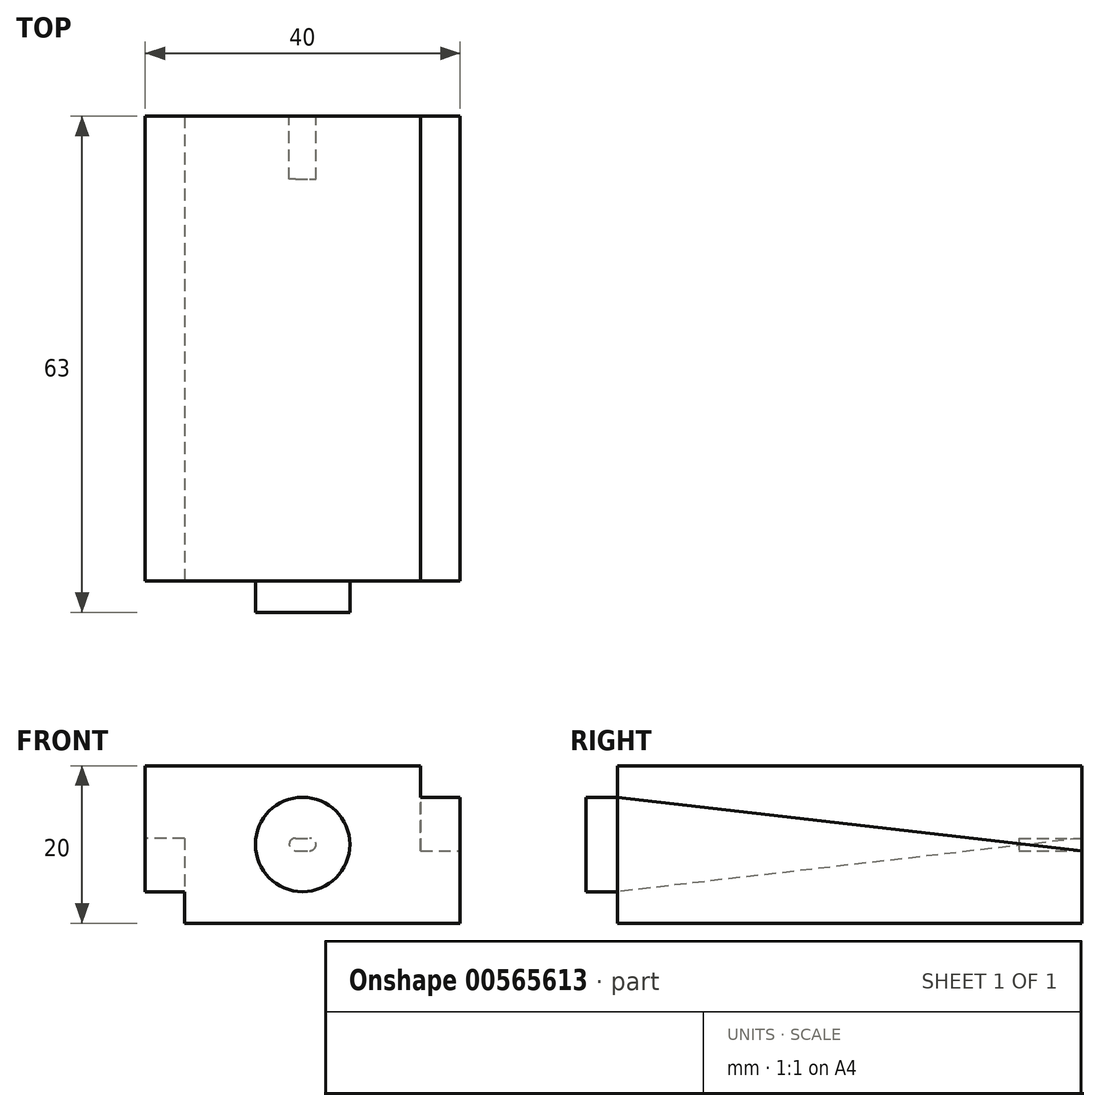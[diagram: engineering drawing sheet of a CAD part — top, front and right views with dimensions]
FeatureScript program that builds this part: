
annotation { "Feature Type Name" : "Feature", "Feature Type Description" : "" }
export const myFeature = defineFeature(function(context is Context, id is Id, definition is map)
    precondition{}
    {
        {
            var Q0;
            Q0=qCreatedBy(makeId("Top.planeOp"),FACE);
            var sketch = newSketch(context, id + "F0", { "sketchPlane" : qUnion([Q0])});
            skLineSegment(sketch, "E0.bottom", {"start": v(-20, 0) * mm, "end": v(20, 0) * mm});
            skLineSegment(sketch, "E0.top", {"start": v(-20, -59) * mm, "end": v(20, -59) * mm});
            skLineSegment(sketch, "E0.left", {"start": v(-20, 0) * mm, "end": v(-20, -59) * mm});
            skLineSegment(sketch, "E0.right", {"start": v(20, 0) * mm, "end": v(20, -59) * mm});
            skSolve(sketch);
        }
        {
            var Q0;
            Q0=makeQuery(id+"F0.imprint","IMPRINT",FACE,{"disambiguationData":[TD([[makeQuery(id+"F0.imprint","IMPRINT",EDGE,{"derivedFrom":sQuery(id+"F0.wireOp",EDGE,"E0.bottom")}),-1.0]])]});
            extrude(context, id + "F1", {"entities" : qUnion([Q0]), "endBound" : BoundingType.SYMMETRIC, "depth" : 20 * mm, "offsetDistance" : 25 * mm});
        }
        {
            var Q0;
            Q0=makeQuery(id+"F1.opExtrude","SWEPT_FACE",FACE,{"disambiguationData":[OSD([sQuery(id+"F0.wireOp",EDGE,"E0.bottom")])]});
            var sketch = newSketch(context, id + "F2", { "sketchPlane" : qUnion([Q0])});
            skLineSegment(sketch, "E1.bottom", {"start": v(0.9, -0.8) * mm, "end": v(-0.9, -0.8) * mm});
            skLineSegment(sketch, "E1.top", {"start": v(0.9, 0.8) * mm, "end": v(-0.9, 0.8) * mm});
            skLineSegment(sketch, "E1.left", {"start": v(0.9, -0.8) * mm, "end": v(0.9, 0.8) * mm, "construction": true});
            skLineSegment(sketch, "E1.right", {"start": v(-0.9, -0.8) * mm, "end": v(-0.9, 0.8) * mm, "construction": true});
            skPoint(sketch, "E1.middle", {"position": v(0, 0) * mm});
            skArc(sketch, "E2", {"start": v(-0.9, 0.8) * mm, "mid": v(-1.7, 0) * mm, "end": v(-0.9, -0.8) * mm});
            skArc(sketch, "E3", {"start": v(0.9, -0.8) * mm, "mid": v(1.7, 0) * mm, "end": v(0.9, 0.8) * mm});
            skSolve(sketch);
        }
        {
            var Q0;
            Q0=makeQuery(id+"F2.imprint","IMPRINT",FACE,{"disambiguationData":[TD([[makeQuery(id+"F2.imprint","IMPRINT",EDGE,{"derivedFrom":sQuery(id+"F2.wireOp",EDGE,"E1.bottom")}),-1.0]])]});
            extrude(context, id + "F3", {"entities" : qUnion([Q0]), "operationType" : NewBodyOperationType.REMOVE, "oppositeDirection" : true, "depth" : 8 * mm, "offsetDistance" : 25 * mm});
        }
        {
            var Q0;
            Q0=makeQuery(id+"F1.opExtrude","SWEPT_FACE",FACE,{"disambiguationData":[OSD([sQuery(id+"F0.wireOp",EDGE,"E0.top")])]});
            var sketch = newSketch(context, id + "F4", { "sketchPlane" : qUnion([Q0])});
            skCircle(sketch, "E4", {"center": v(0, 0) * mm, "radius": 6 * mm});
            skSolve(sketch);
        }
        {
            var Q0;
            Q0=makeQuery(id+"F4.imprint","IMPRINT",FACE,{"disambiguationData":[TD([[makeQuery(id+"F4.imprint","IMPRINT",EDGE,{"derivedFrom":sQuery(id+"F4.wireOp",EDGE,"E4")}),1.0]])]});
            extrude(context, id + "F5", {"entities" : qUnion([Q0]), "operationType" : NewBodyOperationType.ADD, "depth" : 4 * mm, "offsetDistance" : 25 * mm});
        }
        {
            var Q0;
            Q0=makeQuery(id+"F1.opExtrude","SWEPT_FACE",FACE,{"disambiguationData":[OSD([sQuery(id+"F0.wireOp",EDGE,"E0.left")])]});
            var sketch = newSketch(context, id + "F6", { "sketchPlane" : qUnion([Q0])});
            skPoint(sketch, "E5.0", {"position": v(0, 0.8) * mm});
            skLineSegment(sketch, "E6.0", {"start": v(59, 6) * mm, "end": v(59, -6) * mm, "construction": true});
            skLineSegment(sketch, "E7", {"start": v(0, 0.8) * mm, "end": v(59, -6) * mm});
            skLineSegment(sketch, "E8", {"start": v(59, -10) * mm, "end": v(0, -10) * mm});
            skLineSegment(sketch, "E9", {"start": v(0, -10) * mm, "end": v(0, 0.8) * mm});
            skLineSegment(sketch, "E10", {"start": v(59, -6) * mm, "end": v(59, -10) * mm});
            skSolve(sketch);
        }
        {
            var Q0;
            Q0=makeQuery(id+"F6.imprint","IMPRINT",FACE,{"disambiguationData":[TD([[makeQuery(id+"F6.imprint","IMPRINT",EDGE,{"derivedFrom":sQuery(id+"F6.wireOp",EDGE,"E7")}),-1.0]])]});
            extrude(context, id + "F7", {"entities" : qUnion([Q0]), "operationType" : NewBodyOperationType.REMOVE, "oppositeDirection" : true, "depth" : 5 * mm, "offsetDistance" : 25 * mm});
        }
        {
            var Q0;
            Q0=makeQuery(id+"F1.opExtrude","SWEPT_FACE",FACE,{"disambiguationData":[OSD([sQuery(id+"F0.wireOp",EDGE,"E0.right")])]});
            var sketch = newSketch(context, id + "F8", { "sketchPlane" : qUnion([Q0])});
            skPoint(sketch, "E11.0", {"position": v(0, -0.8) * mm});
            skLineSegment(sketch, "E12.0", {"start": v(-59, -6) * mm, "end": v(-59, 6) * mm, "construction": true});
            skLineSegment(sketch, "E13", {"start": v(0, -0.8) * mm, "end": v(-59, 6) * mm});
            skLineSegment(sketch, "E14", {"start": v(-59, 10) * mm, "end": v(0, 10) * mm});
            skLineSegment(sketch, "E15", {"start": v(0, 10) * mm, "end": v(0, -0.8) * mm});
            skLineSegment(sketch, "E16", {"start": v(-59, 10) * mm, "end": v(-59, 6) * mm});
            skSolve(sketch);
        }
        {
            var Q0;
            Q0=makeQuery(id+"F8.imprint","IMPRINT",FACE,{"disambiguationData":[TD([[makeQuery(id+"F8.imprint","IMPRINT",EDGE,{"derivedFrom":sQuery(id+"F8.wireOp",EDGE,"E13")}),-1.0]])]});
            extrude(context, id + "F9", {"entities" : qUnion([Q0]), "operationType" : NewBodyOperationType.REMOVE, "oppositeDirection" : true, "depth" : 5 * mm, "offsetDistance" : 25 * mm});
        }
    });
